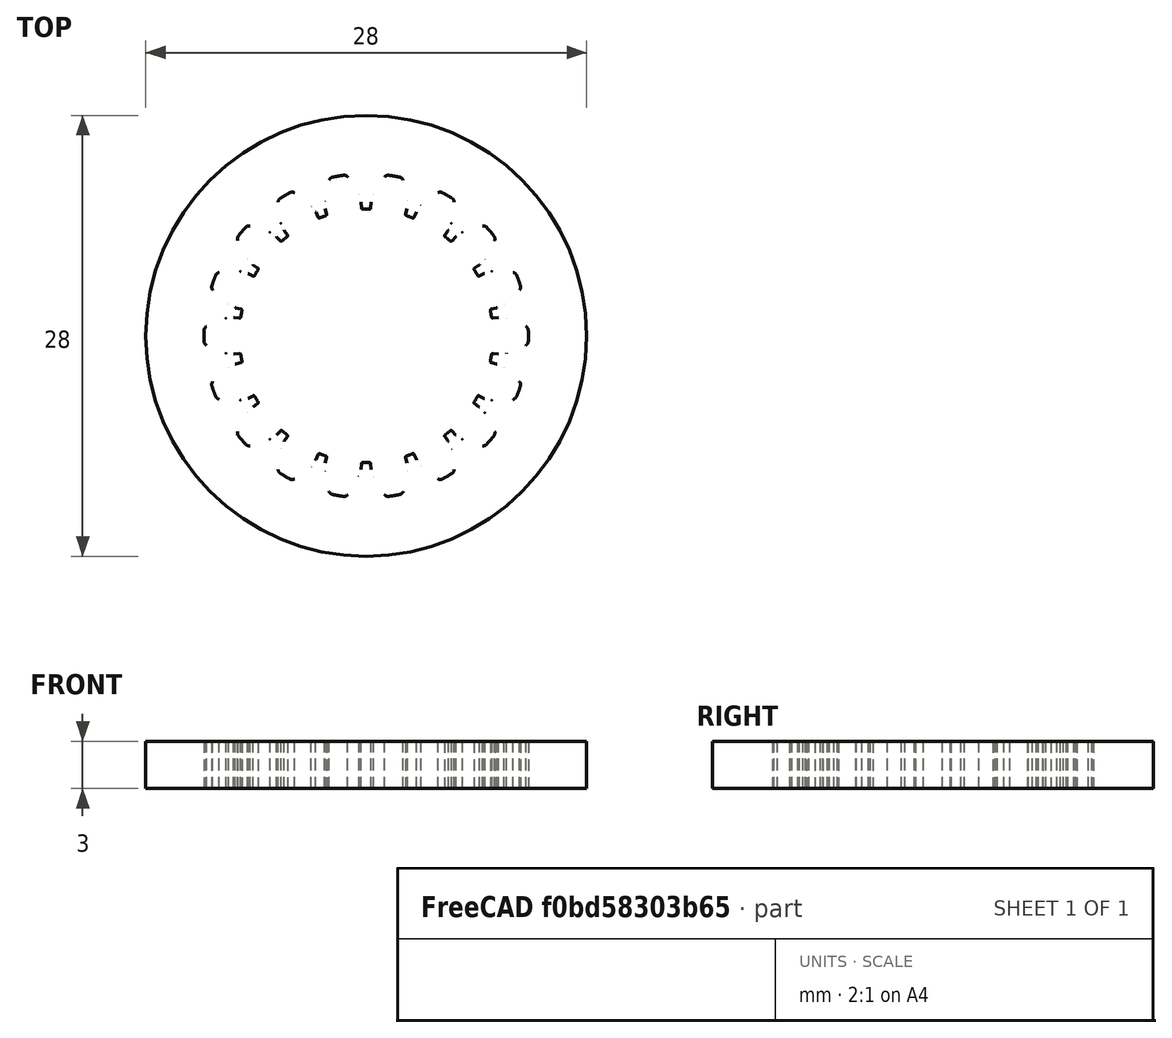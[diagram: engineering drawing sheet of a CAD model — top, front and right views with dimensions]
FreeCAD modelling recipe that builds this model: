
FCSTD DOCUMENT  (FreeCAD 0.19R24276 (Git))
Label: Gear_privod_perehodnik_to_GT2_test_3mm_offset_03
License: All rights reserved
LicenseURL: http://en.wikipedia.org/wiki/All_rights_reserved
objects: Part::Part2DObjectPython×1, Part::Offset2D×1, Part::Cylinder×1, Part::Extrusion×1, Part::Cut×1
note: 5 computed .brp shape members not serialized (recipe doc carries the construction recipe); baked Part::Feature solids carry a one-line shape summary decoded from their .brp

FEATURE [Part::Part2DObjectPython] InvoluteGear  # Draft 2D object (typed FeaturePython)
  ExternalGear = true
  HighPrecision = true
  Modules = 1
  NumberOfTeeth = 18
  PressureAngle = 20
FEATURE [Part::Offset2D] Offset2D
  Fill = false
  Intersection = false
  Join = 0
  Mode = 1
  SelfIntersection = false
  Source = -> InvoluteGear
  Value = 0.3
FEATURE [Part::Cylinder] Cylinder  label="Цилиндр"
  Angle = 360
  AttacherType = Attacher::AttachEngine3D
  Height = 3
  Radius = 14
FEATURE [Part::Extrusion] Extrude
  Base = -> Offset2D
  Dir = (0,0,1)
  DirMode = 2
  FaceMakerClass = Part::FaceMakerBullseye
  LengthFwd = 3
  LengthRev = 0
  Solid = true
  Symmetric = false
FEATURE [Part::Cut] Cut
  Base = -> Cylinder
  Tool = -> Extrude
